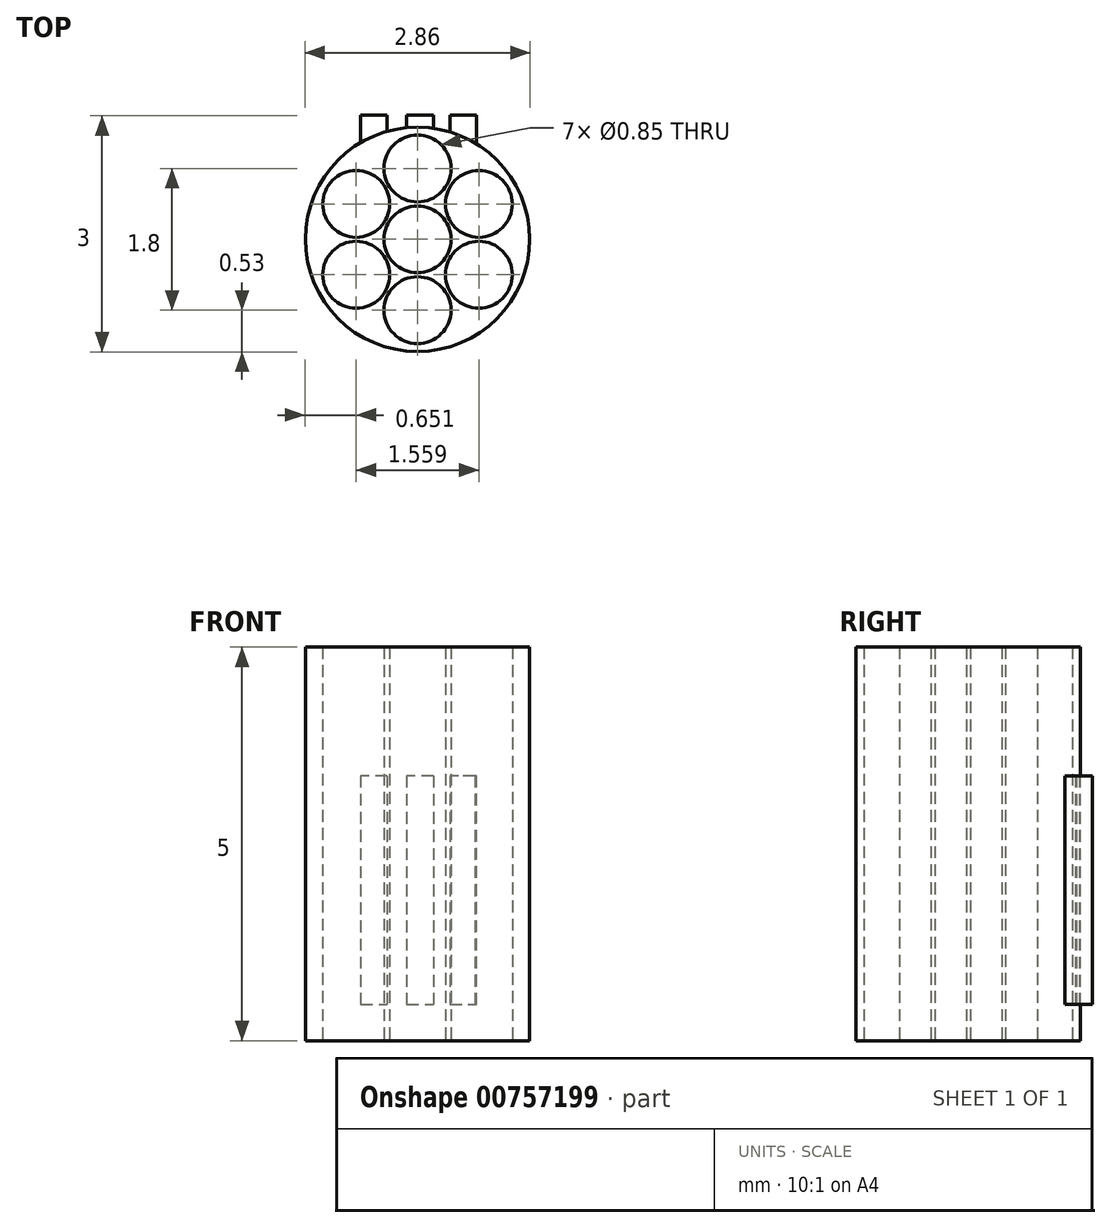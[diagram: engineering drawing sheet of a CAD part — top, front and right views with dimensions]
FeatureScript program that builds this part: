
annotation { "Feature Type Name" : "Feature", "Feature Type Description" : "" }
export const myFeature = defineFeature(function(context is Context, id is Id, definition is map)
    precondition{}
    {
        {
            var Q0;
            Q0=qCreatedBy(makeId("Top.planeOp"),FACE);
            var sketch = newSketch(context, id + "F0", { "sketchPlane" : qUnion([Q0])});
            skCircle(sketch, "E0", {"center": v(0, 0) * mm, "radius": 0.9 * mm});
            skCircle(sketch, "E1.cCircle", {"center": v(0, 0) * mm, "radius": 0.9 * mm, "construction": true});
            skLineSegment(sketch, "E1.0", {"start": v(0, 0.9) * mm, "end": v(0.78, 0.45) * mm});
            skLineSegment(sketch, "E1.1", {"start": v(0.78, 0.45) * mm, "end": v(0.78, -0.45) * mm});
            skLineSegment(sketch, "E1.2", {"start": v(0.78, -0.45) * mm, "end": v(0, -0.9) * mm});
            skLineSegment(sketch, "E1.3", {"start": v(0, -0.9) * mm, "end": v(-0.78, -0.45) * mm});
            skLineSegment(sketch, "E1.4", {"start": v(-0.78, -0.45) * mm, "end": v(-0.78, 0.45) * mm});
            skLineSegment(sketch, "E1.5", {"start": v(-0.78, 0.45) * mm, "end": v(0, 0.9) * mm});
            skSolve(sketch);
        }
        {
            var Q0;
            Q0=qCreatedBy(makeId("Top.planeOp"),FACE);
            var sketch = newSketch(context, id + "F1", { "sketchPlane" : qUnion([Q0])});
            skCircle(sketch, "E2", {"center": v(0, 0) * mm, "radius": 0.42 * mm});
            skCircle(sketch, "E3", {"center": v(0, 0.9) * mm, "radius": 0.42 * mm});
            skCircle(sketch, "E4", {"center": v(0.78, 0.45) * mm, "radius": 0.42 * mm});
            skCircle(sketch, "E5", {"center": v(0.78, -0.45) * mm, "radius": 0.42 * mm});
            skCircle(sketch, "E6", {"center": v(0, -0.9) * mm, "radius": 0.42 * mm});
            skCircle(sketch, "E7", {"center": v(-0.78, -0.45) * mm, "radius": 0.42 * mm});
            skCircle(sketch, "E8", {"center": v(-0.78, 0.45) * mm, "radius": 0.42 * mm});
            skSolve(sketch);
        }
        {
            var Q0;
            Q0=qCreatedBy(makeId("Top.planeOp"),FACE);
            var sketch = newSketch(context, id + "F2", { "sketchPlane" : qUnion([Q0])});
            skCircle(sketch, "E9", {"center": v(0, 0) * mm, "radius": 1.43 * mm});
            skSolve(sketch);
        }
        {
            var Q0;
            Q0=qSketchRegion(id+"F2",true);
            extrude(context, id + "F3", {"entities" : qUnion([Q0]), "depth" : 5 * mm, "offsetDistance" : 25 * mm});
        }
        {
            var Q0;
            Q0=makeQuery(id+"F3.opExtrude","CAP_FACE",FACE,{"disambiguationData":[OSD([sQuery(id+"F2.wireOp",EDGE,"E9")])],"isStart":false});
            var sketch = newSketch(context, id + "F4", { "sketchPlane" : qUnion([Q0])});
            skPoint(sketch, "E10", {"position": v(0, -1.43) * mm});
            skPoint(sketch, "E11", {"position": v(-0.36, -1.43) * mm});
            skPoint(sketch, "E12", {"position": v(0.42, -1.43) * mm});
            skSolve(sketch);
        }
        {
            var Q0;
            Q0=makeQuery(id+"F3.opExtrude","CAP_FACE",FACE,{"disambiguationData":[OSD([sQuery(id+"F2.wireOp",EDGE,"E9")])],"isStart":true});
            var sketch = newSketch(context, id + "F5", { "sketchPlane" : qUnion([Q0])});
            skPoint(sketch, "E13", {"position": v(0, 1.43) * mm});
            skPoint(sketch, "E14", {"position": v(-0.36, 1.43) * mm});
            skPoint(sketch, "E15", {"position": v(0.42, 1.43) * mm});
            skSolve(sketch);
        }
        {
            var Q0;
            Q0=sQuery(id+"F4.wireOp",VERTEX,"E10");
            var Q1;
            Q1=sQuery(id+"F5.wireOp",VERTEX,"E13");
            var Q2;
            Q2=sQuery(id+"F5.wireOp",VERTEX,"E15");
            cPlane(context, id + "F6", {"entities" : qUnion([Q0, Q1, Q2]), "cplaneType" : CPlaneType.THREE_POINT, "offset" : 0 * mm, "oppositeDirection" : true, "width" : 150 * mm, "height" : 150 * mm});
        }
        {
            var Q0;
            Q0=qCreatedBy(id+"F6.planeOp",FACE);
            cPlane(context, id + "F7", {"entities" : qUnion([Q0]), "cplaneType" : CPlaneType.OFFSET, "offset" : 2.65 * mm, "width" : 150 * mm, "height" : 150 * mm});
        }
        {
            var Q0;
            Q0=qCreatedBy(id+"F7.planeOp",FACE);
            var sketch = newSketch(context, id + "F8", { "sketchPlane" : qUnion([Q0])});
            skText(sketch, "E16", { "text": "II", "fontName": "OpenSans-Regular.ttf"});
            skText(sketch, "E17", { "text": "I", "fontName": "OpenSans-Regular.ttf"});
            const initialGuessF8  = {"E16": [-0.00115, 0.00046, 1, 0, 0.00293], "E17": [-0.0006, 0.00046, 1, 0, 0.00293]};
            skSetInitialGuess(sketch, initialGuessF8);
            skSolve(sketch);
        }
        {
            var Q0;
            Q0=qSketchRegion(id+"F8",true);
            extrude(context, id + "F9", {"entities" : qUnion([Q0]), "operationType" : NewBodyOperationType.ADD, "depth" : 0.35 * mm, "offsetDistance" : 25 * mm});
        }
        {
            var Q0;
            Q0=qSketchRegion(id+"F1",true);
            extrude(context, id + "F10", {"entities" : qUnion([Q0]), "operationType" : NewBodyOperationType.REMOVE, "endBound" : BoundingType.THROUGH_ALL, "depth" : 25 * mm, "offsetDistance" : 25 * mm});
        }
    });
